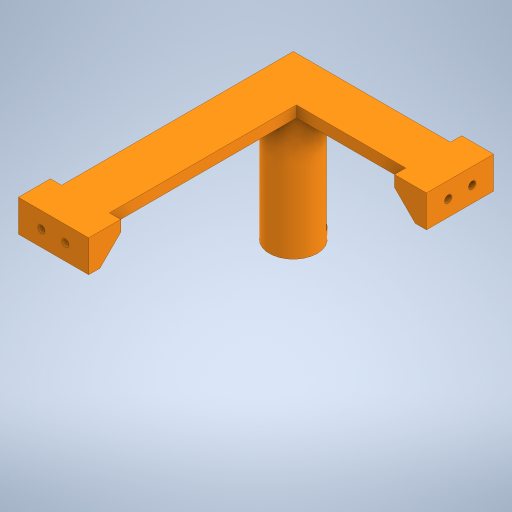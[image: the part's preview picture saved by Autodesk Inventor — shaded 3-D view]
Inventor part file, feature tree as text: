
AUTODESK INVENTOR PART (.ipt)
format: ipt  version: 2023 (Build 270158000, 158)  size: 434,176 bytes
history: native  units: mm
features: extrude x14, sketch x14, other x3, projected_geometry x2, mirror x1, reference x1
ambient origin geometry x8: Origin, YZ Plane, XZ Plane, XY Plane, X Axis, Y Axis, Z Axis, Center Point
bodies: Solid1 (feature_tree)
feature tree (35):
  extrude  "Extrusion1"  Depth=20.0mm
  extrude  "Extrusion2"  Depth=7.0mm
  sketch  "Sketch3"  dims[d4=30.0mm d5=0.0mm d6=80.0mm d7=7.0mm d8=0.0mm d9=0.0mm]
  extrude  "Extrusion3"  Depth=80.0mm TaperAngle=0.0deg
  extrude  "Extrusion4"  Depth=10.0mm
  extrude  "Extrusion5"  Depth=10.0mm
  extrude  "Extrusion6"  Depth=15.0mm
  extrude  "Extrusion7"  Depth=7.0mm TaperAngle=0.0deg
  extrude  "Extrusion8"  Depth=7.0mm TaperAngle=0.0deg
  extrude  "Extrusion9"  Depth=11.0mm
  extrude  "Extrusion10"  Depth=80.0mm
  extrude  "Extrusion11"  Depth=7.0mm TaperAngle=0.0deg
  extrude  "Extrusion12"  Depth=15.0mm
  extrude  "Extrusion13"  Depth=7.0mm TaperAngle=0.0deg
  mirror  "Mirror1"
  extrude  "Extrusion14"  TaperAngle=0.0deg  [1 undecoded]
  sketch  "Sketch1"  dims[d0=7.0mm d1=20.0mm]
  sketch  "Sketch2"  dims[d2=7.0mm d3=150.0mm]
  sketch  "Sketch4"  dims[d10=10.0mm d11=4.5mm]
  projected_geometry  "Projected Loop1"
  sketch  "Sketch5"  dims[d12=4.5mm d13=10.0mm]
  projected_geometry  "Projected Loop2"
  sketch  "Sketch6"  dims[d14=15.0mm d15=7.5mm]
  sketch  "Sketch7"  dims[d16=13.0mm d17=7.0mm d18=0.0mm]
  sketch  "Sketch8"  dims[d19=7.0mm d20=0.0mm d21=7.0mm d22=0.0mm]
  reference  "Reference1"
  sketch  "Sketch9"  dims[d23=11.0mm d24=11.0mm]
  sketch  "Sketch10"  dims[d25=12.0mm d26=0.0mm d27=80.0mm]
  sketch  "Sketch11"  dims[d28=7.0mm d29=72.0mm d30=0.0mm]
  sketch  "Sketch13"  dims[d31=0.0mm d32=15.0mm]
  sketch  "Sketch15"  dims[d33=20.0mm d34=7.0mm d35=0.0mm]
  sketch  "Sketch16"  dims[d36=7.0mm d37=0.0mm d38=7.0mm d39=7.0mm d40=13.0mm d41=7.0mm d42=0.0mm d43=0.0mm d44=45.0deg d45=7.0mm d46=0.0mm d47=7.0mm d48=0.0mm d49=10.0mm d50=10.0mm d51=15.0mm d52=6.5mm d53=6.507214mm d54=4.5mm d55=4.5mm d56=7.0mm d57=0.0mm d58=10.0mm d59=10.0mm d60=20.0mm d61=0.0mm d62=400.0mm d63=0.0mm]
  other  "<userpath>\OneDrive\ClawdDrive\Objet3D\3DPrinter\inventor\3DPrinterBeltCoreXY.iam"
  other  "3DPrinterBeltCoreXY.iam"
  other  "20X20 - T-slot - Vertical:2"
note: 1 required parameter value undecoded (feature->parameter linkage not recoverable at this tier; creation-order binding heuristic only, values carry confidence <= 0.55)
